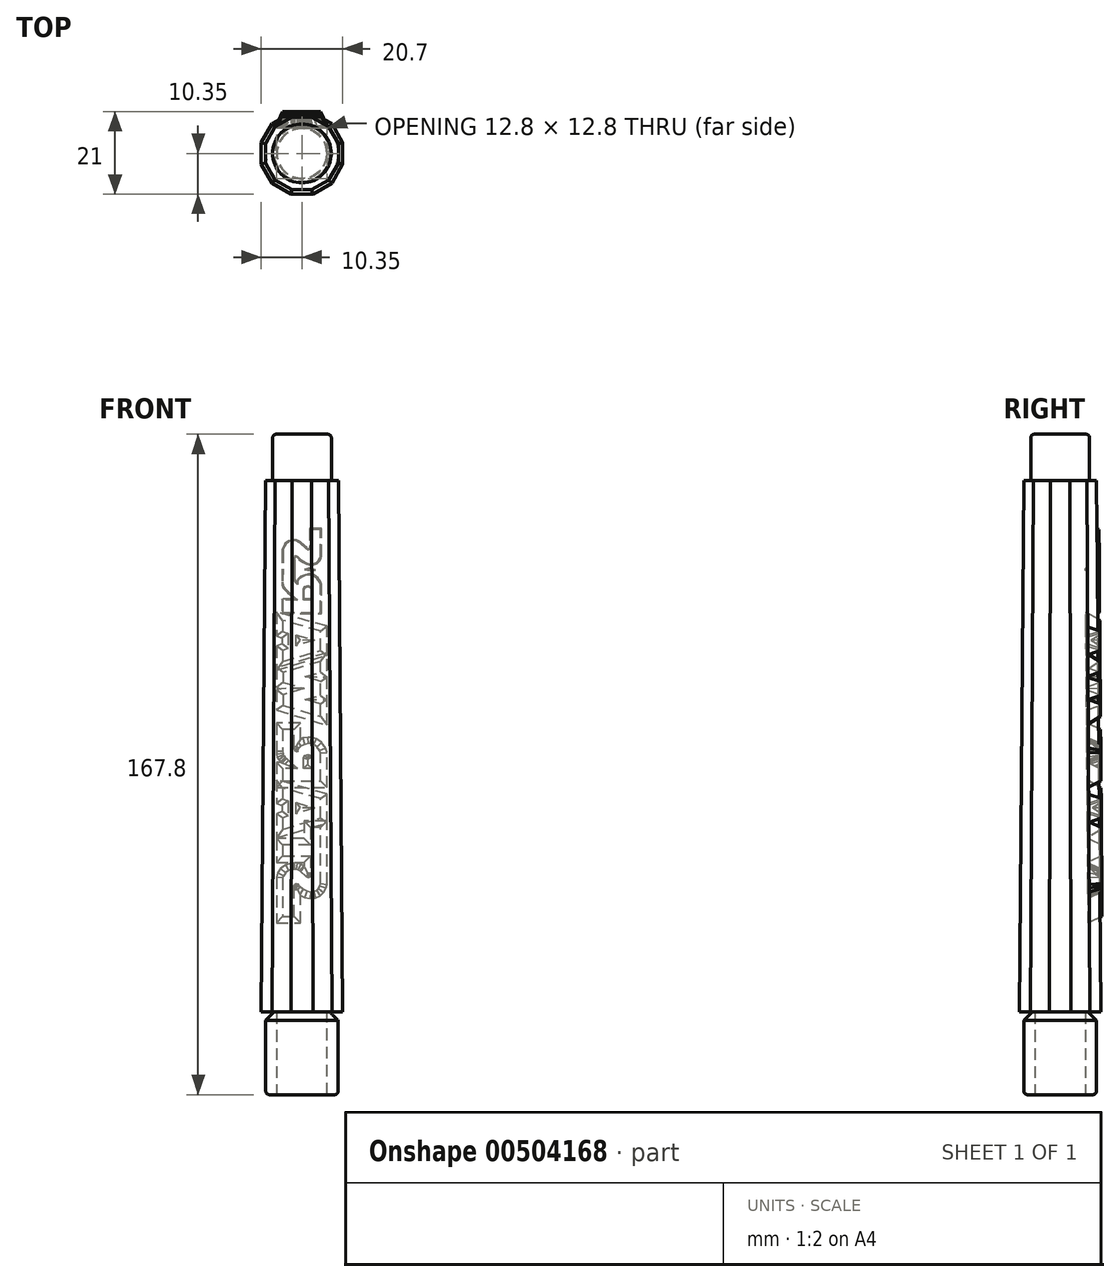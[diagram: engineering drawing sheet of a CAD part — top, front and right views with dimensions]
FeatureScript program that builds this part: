
annotation { "Feature Type Name" : "Feature", "Feature Type Description" : "" }
export const myFeature = defineFeature(function(context is Context, id is Id, definition is map)
    precondition{}
    {
        {
            var Q0;
            Q0=qCreatedBy(makeId("Top.planeOp"),FACE);
            var sketch = newSketch(context, id + "F0", { "sketchPlane" : qUnion([Q0])});
            skCircle(sketch, "E0", {"center": v(0, 0) * mm, "radius": 6.4 * mm});
            skCircle(sketch, "E1", {"center": v(0, 0) * mm, "radius": 9.2 * mm});
            skCircle(sketch, "E2", {"center": v(0, 0) * mm, "radius": 10.35 * mm});
            skSolve(sketch);
        }
        {
            var Q0;
            Q0=qCreatedBy(makeId("Top.planeOp"),FACE);
            cPlane(context, id + "F1", {"entities" : qUnion([Q0]), "cplaneType" : CPlaneType.OFFSET, "offset" : 21 * mm, "width" : 150 * mm, "height" : 150 * mm});
        }
        {
            var Q0;
            Q0=qCreatedBy(id+"F1.planeOp",FACE);
            var sketch = newSketch(context, id + "F2", { "sketchPlane" : qUnion([Q0])});
            skCircle(sketch, "E3", {"center": v(0, 0) * mm, "radius": 6.4 * mm});
            skCircle(sketch, "E4", {"center": v(0, 0) * mm, "radius": 9.2 * mm});
            skCircle(sketch, "E5", {"center": v(0, 0) * mm, "radius": 10.35 * mm});
            skSolve(sketch);
        }
        {
            var Q0;
            Q0=qCreatedBy(id+"F1.planeOp",FACE);
            cPlane(context, id + "F3", {"entities" : qUnion([Q0]), "cplaneType" : CPlaneType.OFFSET, "offset" : 135 * mm, "width" : 150 * mm, "height" : 150 * mm});
        }
        {
            var Q0;
            Q0=qCreatedBy(id+"F3.planeOp",FACE);
            var sketch = newSketch(context, id + "F4", { "sketchPlane" : qUnion([Q0])});
            skPoint(sketch, "E6.0", {"position": v(0, 0) * mm});
            skCircle(sketch, "E7", {"center": v(0, 0) * mm, "radius": 4.9 * mm});
            skCircle(sketch, "E8", {"center": v(0, 0) * mm, "radius": 7.45 * mm});
            skCircle(sketch, "E9", {"center": v(0, 0) * mm, "radius": 9.25 * mm});
            skSolve(sketch);
        }
        {
            var Q0;
            Q0=qCreatedBy(id+"F3.planeOp",FACE);
            cPlane(context, id + "F5", {"entities" : qUnion([Q0]), "cplaneType" : CPlaneType.OFFSET, "offset" : 11.8 * mm, "width" : 150 * mm, "height" : 150 * mm});
        }
        {
            var Q0;
            Q0=qCreatedBy(id+"F5.planeOp",FACE);
            var sketch = newSketch(context, id + "F6", { "sketchPlane" : qUnion([Q0])});
            skPoint(sketch, "E10.0", {"position": v(0, 0) * mm});
            skCircle(sketch, "E11", {"center": v(0, 0) * mm, "radius": 4.9 * mm});
            skCircle(sketch, "E12", {"center": v(0, 0) * mm, "radius": 7.45 * mm});
            skCircle(sketch, "E13", {"center": v(0, 0) * mm, "radius": 9.25 * mm});
            skSolve(sketch);
        }
        {
            var Q0;
            Q0=qCreatedBy(makeId("Front.planeOp"),FACE);
            var sketch = newSketch(context, id + "F7", { "sketchPlane" : qUnion([Q0])});
            skPoint(sketch, "E14.0", {"position": v(0, 167.8) * mm});
            skLineSegment(sketch, "E15", {"start": v(0, 167.8) * mm, "end": v(0, 0) * mm, "construction": true});
            skCircle(sketch, "E16", {"center": v(0, 36.85) * mm, "radius": 2.35 * mm});
            skCircle(sketch, "E17", {"center": v(0, 57.2) * mm, "radius": 2.6 * mm});
            skCircle(sketch, "E18", {"center": v(0, 79.25) * mm, "radius": 2.75 * mm});
            skCircle(sketch, "E19", {"center": v(0, 102.2) * mm, "radius": 2.3 * mm});
            skCircle(sketch, "E20", {"center": v(0, 127.6) * mm, "radius": 3 * mm});
            skCircle(sketch, "E21", {"center": v(2.3, 147.6) * mm, "radius": 2.1 * mm});
            skCircle(sketch, "E22", {"center": v(-3.01, 148.25) * mm, "radius": 1.45 * mm});
            skCircle(sketch, "E23", {"center": v(0, 30.75) * mm, "radius": 2.75 * mm});
            skSolve(sketch);
        }
        {
            var Q0;
            Q0=makeQuery(id+"F0.imprint","IMPRINT",FACE,{"disambiguationData":[TD([[makeQuery(id+"F0.imprint","IMPRINT",EDGE,{"derivedFrom":sQuery(id+"F0.wireOp",EDGE,"E0")}),1.0]])]});
            var Q1;
            Q1=makeQuery(id+"F2.imprint","IMPRINT",FACE,{"disambiguationData":[TD([[makeQuery(id+"F2.imprint","IMPRINT",EDGE,{"derivedFrom":sQuery(id+"F2.wireOp",EDGE,"E3")}),1.0]])]});
            var Q2;
            Q2=makeQuery(id+"F4.imprint","IMPRINT",FACE,{"disambiguationData":[TD([[makeQuery(id+"F4.imprint","IMPRINT",EDGE,{"derivedFrom":sQuery(id+"F4.wireOp",EDGE,"E7")}),1.0]])]});
            var Q3;
            Q3=makeQuery(id+"F6.imprint","IMPRINT",FACE,{"disambiguationData":[TD([[makeQuery(id+"F6.imprint","IMPRINT",EDGE,{"derivedFrom":sQuery(id+"F6.wireOp",EDGE,"E11")}),1.0]])]});
            loft(context, id + "F8", {"sheetProfilesArray" : [{ "sheetProfileEntities" : qUnion([Q0]) }, { "sheetProfileEntities" : qUnion([Q1]) }, { "sheetProfileEntities" : qUnion([Q2]) }, { "sheetProfileEntities" : qUnion([Q3]) }]});
        }
        {
            var Q0;
            Q0=makeQuery(id+"F7.imprint","IMPRINT",FACE,{"disambiguationData":[TD([[makeQuery(id+"F7.imprint","IMPRINT",EDGE,{"derivedFrom":sQuery(id+"F7.wireOp",EDGE,"E23")}),1.0]])]});
            extrude(context, id + "F9", {"entities" : qUnion([Q0]), "operationType" : NewBodyOperationType.ADD, "oppositeDirection" : true, "depth" : 15 * mm});
        }
        {
            var Q0;
            Q0=makeQuery(id+"F7.imprint","IMPRINT",FACE,{"disambiguationData":[TD([[makeQuery(id+"F7.imprint","IMPRINT",EDGE,{"derivedFrom":sQuery(id+"F7.wireOp",EDGE,"E16")}),1.0]])]});
            var Q1;
            Q1=makeQuery(id+"F7.imprint","IMPRINT",FACE,{"disambiguationData":[TD([[makeQuery(id+"F7.imprint","IMPRINT",EDGE,{"derivedFrom":sQuery(id+"F7.wireOp",EDGE,"E17")}),1.0]])]});
            var Q2;
            Q2=makeQuery(id+"F7.imprint","IMPRINT",FACE,{"disambiguationData":[TD([[makeQuery(id+"F7.imprint","IMPRINT",EDGE,{"derivedFrom":sQuery(id+"F7.wireOp",EDGE,"E18")}),1.0]])]});
            var Q3;
            Q3=makeQuery(id+"F7.imprint","IMPRINT",FACE,{"disambiguationData":[TD([[makeQuery(id+"F7.imprint","IMPRINT",EDGE,{"derivedFrom":sQuery(id+"F7.wireOp",EDGE,"E19")}),1.0]])]});
            var Q4;
            Q4=makeQuery(id+"F7.imprint","IMPRINT",FACE,{"disambiguationData":[TD([[makeQuery(id+"F7.imprint","IMPRINT",EDGE,{"derivedFrom":sQuery(id+"F7.wireOp",EDGE,"E20")}),1.0]])]});
            var Q5;
            Q5=makeQuery(id+"F7.imprint","IMPRINT",FACE,{"disambiguationData":[TD([[makeQuery(id+"F7.imprint","IMPRINT",EDGE,{"derivedFrom":sQuery(id+"F7.wireOp",EDGE,"E21")}),1.0]])]});
            var Q6;
            Q6=makeQuery(id+"F7.imprint","IMPRINT",FACE,{"disambiguationData":[TD([[makeQuery(id+"F7.imprint","IMPRINT",EDGE,{"derivedFrom":sQuery(id+"F7.wireOp",EDGE,"E22")}),1.0]])]});
            extrude(context, id + "F10", {"entities" : qUnion([Q0, Q1, Q2, Q3, Q4, Q5, Q6]), "operationType" : NewBodyOperationType.ADD, "depth" : 15 * mm});
        }
        {
            var Q0;
            Q0=makeQuery(id+"F0.imprint","IMPRINT",FACE,{"disambiguationData":[TD([[makeQuery(id+"F0.imprint","IMPRINT",EDGE,{"derivedFrom":sQuery(id+"F0.wireOp",EDGE,"E0")}),-1.0]])]});
            var Q1;
            Q1=makeQuery(id+"F0.imprint","IMPRINT",FACE,{"disambiguationData":[TD([[makeQuery(id+"F0.imprint","IMPRINT",EDGE,{"derivedFrom":sQuery(id+"F0.wireOp",EDGE,"E0")}),1.0]])]});
            extrude(context, id + "F11", {"entities" : qUnion([Q0, Q1]), "depth" : 21 * mm});
        }
        {
            var Q0;
            Q0=makeQuery(id+"F6.imprint","IMPRINT",FACE,{"disambiguationData":[TD([[makeQuery(id+"F6.imprint","IMPRINT",EDGE,{"derivedFrom":sQuery(id+"F6.wireOp",EDGE,"E11")}),-1.0]])]});
            var Q1;
            Q1=makeQuery(id+"F6.imprint","IMPRINT",FACE,{"disambiguationData":[TD([[makeQuery(id+"F6.imprint","IMPRINT",EDGE,{"derivedFrom":sQuery(id+"F6.wireOp",EDGE,"E11")}),1.0]])]});
            extrude(context, id + "F12", {"entities" : qUnion([Q0, Q1]), "oppositeDirection" : true, "depth" : 11.8 * mm});
        }
        {
            var Q0;
            Q0=qCreatedBy(id+"F1.planeOp",FACE);
            var sketch = newSketch(context, id + "F13", { "sketchPlane" : qUnion([Q0])});
            skPoint(sketch, "E24.0", {"position": v(0, 0) * mm});
            skLineSegment(sketch, "E25.0", {"start": v(-2.77, 10.35) * mm, "end": v(2.77, 10.35) * mm});
            skLineSegment(sketch, "E25.1", {"start": v(2.77, 10.35) * mm, "end": v(7.58, 7.58) * mm});
            skLineSegment(sketch, "E25.2", {"start": v(7.58, 7.58) * mm, "end": v(10.35, 2.77) * mm});
            skLineSegment(sketch, "E25.3", {"start": v(10.35, 2.77) * mm, "end": v(10.35, -2.77) * mm});
            skLineSegment(sketch, "E25.4", {"start": v(10.35, -2.77) * mm, "end": v(7.58, -7.58) * mm});
            skLineSegment(sketch, "E25.5", {"start": v(7.58, -7.58) * mm, "end": v(2.77, -10.35) * mm});
            skLineSegment(sketch, "E25.6", {"start": v(2.77, -10.35) * mm, "end": v(-2.77, -10.35) * mm});
            skLineSegment(sketch, "E25.7", {"start": v(-2.77, -10.35) * mm, "end": v(-7.58, -7.58) * mm});
            skLineSegment(sketch, "E25.8", {"start": v(-7.58, -7.58) * mm, "end": v(-10.35, -2.77) * mm});
            skLineSegment(sketch, "E25.9", {"start": v(-10.35, -2.77) * mm, "end": v(-10.35, 2.77) * mm});
            skLineSegment(sketch, "E25.10", {"start": v(-10.35, 2.77) * mm, "end": v(-7.58, 7.58) * mm});
            skLineSegment(sketch, "E25.11", {"start": v(-7.58, 7.58) * mm, "end": v(-2.77, 10.35) * mm});
            skPoint(sketch, "E25.0.midPoint", {"position": v(0, 10.35) * mm});
            skSolve(sketch);
        }
        {
            var Q0;
            Q0=qCreatedBy(id+"F3.planeOp",FACE);
            var sketch = newSketch(context, id + "F14", { "sketchPlane" : qUnion([Q0])});
            skPoint(sketch, "E26.0", {"position": v(0, 0) * mm});
            skLineSegment(sketch, "E27.0", {"start": v(-2.48, 9.25) * mm, "end": v(2.48, 9.25) * mm});
            skLineSegment(sketch, "E27.1", {"start": v(2.48, 9.25) * mm, "end": v(6.77, 6.77) * mm});
            skLineSegment(sketch, "E27.2", {"start": v(6.77, 6.77) * mm, "end": v(9.25, 2.48) * mm});
            skLineSegment(sketch, "E27.3", {"start": v(9.25, 2.48) * mm, "end": v(9.25, -2.48) * mm});
            skLineSegment(sketch, "E27.4", {"start": v(9.25, -2.48) * mm, "end": v(6.77, -6.77) * mm});
            skLineSegment(sketch, "E27.5", {"start": v(6.77, -6.77) * mm, "end": v(2.48, -9.25) * mm});
            skLineSegment(sketch, "E27.6", {"start": v(2.48, -9.25) * mm, "end": v(-2.48, -9.25) * mm});
            skLineSegment(sketch, "E27.7", {"start": v(-2.48, -9.25) * mm, "end": v(-6.77, -6.77) * mm});
            skLineSegment(sketch, "E27.8", {"start": v(-6.77, -6.77) * mm, "end": v(-9.25, -2.48) * mm});
            skLineSegment(sketch, "E27.9", {"start": v(-9.25, -2.48) * mm, "end": v(-9.25, 2.48) * mm});
            skLineSegment(sketch, "E27.10", {"start": v(-9.25, 2.48) * mm, "end": v(-6.77, 6.77) * mm});
            skLineSegment(sketch, "E27.11", {"start": v(-6.77, 6.77) * mm, "end": v(-2.48, 9.25) * mm});
            skPoint(sketch, "E27.0.midPoint", {"position": v(0, 9.25) * mm});
            skSolve(sketch);
        }
        {
            var Q0;
            Q0=makeQuery(id+"F13.imprint","IMPRINT",FACE,{"disambiguationData":[TD([[makeQuery(id+"F13.imprint","IMPRINT",EDGE,{"derivedFrom":sQuery(id+"F13.wireOp",EDGE,"E25.0")}),-1.0]])]});
            var Q1;
            Q1=makeQuery(id+"F14.imprint","IMPRINT",FACE,{"disambiguationData":[TD([[makeQuery(id+"F14.imprint","IMPRINT",EDGE,{"derivedFrom":sQuery(id+"F14.wireOp",EDGE,"E27.0")}),-1.0]])]});
            loft(context, id + "F15", {"sheetProfilesArray" : [{ "sheetProfileEntities" : qUnion([Q0]) }, { "sheetProfileEntities" : qUnion([Q1]) }]});
        }
        {
            var Q0;
            Q0=makeQuery(id+"F8.opLoft","SWEPT_BODY",BODY,{"disambiguationData":[OSD([makeQuery(id+"F0.imprint","IMPRINT",FACE,{"disambiguationData":[TD([[makeQuery(id+"F0.imprint","IMPRINT",EDGE,{"derivedFrom":sQuery(id+"F0.wireOp",EDGE,"E0")}),1.0]])]}),sQuery(id+"F2.wireOp",EDGE,"E3"),sQuery(id+"F4.wireOp",EDGE,"E7"),makeQuery(id+"F6.imprint","IMPRINT",FACE,{"disambiguationData":[TD([[makeQuery(id+"F6.imprint","IMPRINT",EDGE,{"derivedFrom":sQuery(id+"F6.wireOp",EDGE,"E11")}),1.0]])]})])]});
            var Q1;
            Q1=makeQuery(id+"F11.opExtrude","SWEPT_BODY",BODY,{"disambiguationData":[OSD([sQuery(id+"F0.wireOp",EDGE,"E1")])]});
            booleanBodies(context, id + "F16", {"operationType" : BooleanOperationType.SUBTRACTION, "tools" : qUnion([Q0]), "targets" : qUnion([Q1])});
        }
        {
            var Q0;
            Q0=qCreatedBy(makeId("Right.planeOp"),FACE);
            var sketch = newSketch(context, id + "F17", { "sketchPlane" : qUnion([Q0])});
            skPoint(sketch, "E28.0", {"position": v(-8.22, 147.6) * mm});
            skLineSegment(sketch, "E29", {"start": v(-8.22, 147.6) * mm, "end": v(-17.72, 147.6) * mm});
            skCircle(sketch, "E30", {"center": v(-17.72, 147.6) * mm, "radius": 10 * mm});
            skSolve(sketch);
        }
        {
            var Q0;
            Q0=makeQuery(id+"F17.imprint","IMPRINT",FACE,{"disambiguationData":[TD([[makeQuery(id+"F17.imprint","IMPRINT",EDGE,{"derivedFrom":sQuery(id+"F17.wireOp",EDGE,"E30")}),1.0]])]});
            extrude(context, id + "F18", {"entities" : qUnion([Q0]), "endBound" : BoundingType.SYMMETRIC, "oppositeDirection" : true, "depth" : 15 * mm});
        }
        {
            var Q0;
            Q0=makeQuery(id+"F18.opExtrude","SWEPT_BODY",BODY,{"disambiguationData":[OSD([sQuery(id+"F17.wireOp",EDGE,"E30")])]});
            var Q1;
            Q1=makeQuery(id+"F11.opExtrude","SWEPT_BODY",BODY,{"disambiguationData":[OSD([sQuery(id+"F0.wireOp",EDGE,"E1")])]});
            booleanBodies(context, id + "F19", {"operationType" : BooleanOperationType.SUBTRACTION, "tools" : qUnion([Q0]), "targets" : qUnion([Q1])});
        }
        {
            var Q0;
            Q0=makeQuery(id+"F11.opExtrude","CAP_EDGE",EDGE,{"disambiguationData":[OSD([sQuery(id+"F0.wireOp",EDGE,"E1")])],"isStart":false});
            chamfer(context, id + "F20", {"entities" : qUnion([Q0]), "width" : 2.15 * mm, "tangentPropagation" : true});
        }
        {
            var Q0;
            Q0=makeQuery(id+"F12.opExtrude","CAP_EDGE",EDGE,{"disambiguationData":[OSD([sQuery(id+"F6.wireOp",EDGE,"E12")])],"isStart":true});
            var Q1;
            Q1=makeQuery(id+"F11.opExtrude","CAP_EDGE",EDGE,{"disambiguationData":[OSD([sQuery(id+"F0.wireOp",EDGE,"E1")])],"isStart":true});
            fillet(context, id + "F21", {"entities" : qUnion([Q0, Q1]), "radius" : 0.9 * mm, "tangentPropagation" : true, "allowEdgeOverflow" : false});
        }
        {
            var Q0;
            Q0=makeQuery(id+"F15.opLoft","SWEPT_FACE",FACE,{"disambiguationData":[OSD([sQuery(id+"F13.wireOp",EDGE,"E25.0"),sQuery(id+"F13.wireOp",EDGE,"E25.1"),sQuery(id+"F13.wireOp",EDGE,"E25.11"),sQuery(id+"F14.wireOp",EDGE,"E27.0"),sQuery(id+"F14.wireOp",EDGE,"E27.1"),sQuery(id+"F14.wireOp",EDGE,"E27.11")])]});
            var sketch = newSketch(context, id + "F22", { "sketchPlane" : qUnion([Q0])});
            skLineSegment(sketch, "E31", {"start": v(-1.96, 139.37) * mm, "end": v(-1.96, 139.26) * mm});
            skLineSegment(sketch, "E32", {"start": v(-1.96, 139.26) * mm, "end": v(-1.94, 138.93) * mm});
            skLineSegment(sketch, "E33", {"start": v(-1.94, 138.93) * mm, "end": v(-1.84, 138.6) * mm});
            skLineSegment(sketch, "E34", {"start": v(-1.84, 138.6) * mm, "end": v(-1.62, 138.53) * mm});
            skLineSegment(sketch, "E35", {"start": v(-1.62, 138.53) * mm, "end": v(-1.3, 138.74) * mm});
            skLineSegment(sketch, "E36", {"start": v(-1.3, 138.74) * mm, "end": v(-1.22, 138.83) * mm});
            skLineSegment(sketch, "E37", {"start": v(-1.22, 138.83) * mm, "end": v(0.26, 140.08) * mm});
            skLineSegment(sketch, "E38", {"start": v(0.26, 140.08) * mm, "end": v(0.4, 140.21) * mm});
            skLineSegment(sketch, "E39", {"start": v(0.4, 140.21) * mm, "end": v(0.87, 140.56) * mm});
            skLineSegment(sketch, "E40", {"start": v(0.87, 140.56) * mm, "end": v(1.35, 140.8) * mm});
            skLineSegment(sketch, "E41", {"start": v(1.35, 140.8) * mm, "end": v(1.8, 140.88) * mm});
            skLineSegment(sketch, "E42", {"start": v(1.8, 140.88) * mm, "end": v(2.15, 140.9) * mm});
            skLineSegment(sketch, "E43", {"start": v(2.15, 140.9) * mm, "end": v(2.27, 140.9) * mm});
            skLineSegment(sketch, "E44", {"start": v(2.27, 140.9) * mm, "end": v(2.57, 140.9) * mm});
            skLineSegment(sketch, "E45", {"start": v(2.57, 140.9) * mm, "end": v(3.44, 140.6) * mm});
            skLineSegment(sketch, "E46", {"start": v(3.44, 140.6) * mm, "end": v(4.32, 139.89) * mm});
            skLineSegment(sketch, "E47", {"start": v(4.32, 139.89) * mm, "end": v(4.87, 138.96) * mm});
            skLineSegment(sketch, "E48", {"start": v(4.87, 138.96) * mm, "end": v(5.07, 138.27) * mm});
            skLineSegment(sketch, "E49", {"start": v(5.07, 138.27) * mm, "end": v(5.07, 138.03) * mm});
            skLineSegment(sketch, "E50", {"start": v(5.07, 138.03) * mm, "end": v(5.12, 130.13) * mm});
            skLineSegment(sketch, "E51", {"start": v(5.12, 130.13) * mm, "end": v(5.12, 129.96) * mm});
            skLineSegment(sketch, "E52", {"start": v(5.12, 129.96) * mm, "end": v(5.1, 129.47) * mm});
            skLineSegment(sketch, "E53", {"start": v(5.1, 129.47) * mm, "end": v(5, 129.04) * mm});
            skLineSegment(sketch, "E54", {"start": v(5, 129.04) * mm, "end": v(4.75, 128.66) * mm});
            skLineSegment(sketch, "E55", {"start": v(4.75, 128.66) * mm, "end": v(4.43, 128.28) * mm});
            skLineSegment(sketch, "E56", {"start": v(4.43, 128.28) * mm, "end": v(4.32, 128.16) * mm});
            skLineSegment(sketch, "E57", {"start": v(4.32, 128.16) * mm, "end": v(4.15, 127.98) * mm});
            skLineSegment(sketch, "E58", {"start": v(4.15, 127.98) * mm, "end": v(3.6, 127.46) * mm});
            skLineSegment(sketch, "E59", {"start": v(3.6, 127.46) * mm, "end": v(2.77, 126.69) * mm});
            skLineSegment(sketch, "E60", {"start": v(2.77, 126.69) * mm, "end": v(2.07, 126.07) * mm});
            skLineSegment(sketch, "E61", {"start": v(2.07, 126.07) * mm, "end": v(1.77, 125.82) * mm});
            skLineSegment(sketch, "E62", {"start": v(1.77, 125.82) * mm, "end": v(5.12, 125.82) * mm});
            skLineSegment(sketch, "E63", {"start": v(5.12, 125.82) * mm, "end": v(5.12, 122.2) * mm});
            skLineSegment(sketch, "E64", {"start": v(5.12, 122.2) * mm, "end": v(-4.92, 122.2) * mm});
            skLineSegment(sketch, "E65", {"start": v(-4.92, 122.2) * mm, "end": v(-4.92, 123.14) * mm});
            skLineSegment(sketch, "E66", {"start": v(-4.92, 123.14) * mm, "end": v(-4.92, 125.29) * mm});
            skLineSegment(sketch, "E67", {"start": v(-4.92, 125.29) * mm, "end": v(-4.92, 127.67) * mm});
            skLineSegment(sketch, "E68", {"start": v(-4.92, 127.67) * mm, "end": v(-4.92, 128.9) * mm});
            skLineSegment(sketch, "E69", {"start": v(-4.92, 128.9) * mm, "end": v(-4.92, 129.32) * mm});
            skLineSegment(sketch, "E70", {"start": v(-4.92, 129.32) * mm, "end": v(-4.92, 129.57) * mm});
            skLineSegment(sketch, "E71", {"start": v(-4.92, 129.57) * mm, "end": v(-4.68, 130.3) * mm});
            skLineSegment(sketch, "E72", {"start": v(-4.68, 130.3) * mm, "end": v(-4.02, 131.23) * mm});
            skLineSegment(sketch, "E73", {"start": v(-4.02, 131.23) * mm, "end": v(-3.07, 131.91) * mm});
            skLineSegment(sketch, "E74", {"start": v(-3.07, 131.91) * mm, "end": v(-2.2, 132.18) * mm});
            skLineSegment(sketch, "E75", {"start": v(-2.2, 132.18) * mm, "end": v(-1.9, 132.18) * mm});
            skLineSegment(sketch, "E76", {"start": v(-1.9, 132.18) * mm, "end": v(-1.61, 132.18) * mm});
            skLineSegment(sketch, "E77", {"start": v(-1.61, 132.18) * mm, "end": v(-0.72, 132.01) * mm});
            skLineSegment(sketch, "E78", {"start": v(-0.72, 132.01) * mm, "end": v(0.3, 131.56) * mm});
            skLineSegment(sketch, "E79", {"start": v(0.3, 131.56) * mm, "end": v(1.03, 130.9) * mm});
            skLineSegment(sketch, "E80", {"start": v(1.03, 130.9) * mm, "end": v(1.3, 130.32) * mm});
            skLineSegment(sketch, "E81", {"start": v(1.3, 130.32) * mm, "end": v(1.3, 130.13) * mm});
            skLineSegment(sketch, "E82", {"start": v(1.3, 130.13) * mm, "end": v(1.38, 130.21) * mm});
            skLineSegment(sketch, "E83", {"start": v(1.38, 130.21) * mm, "end": v(1.55, 130.46) * mm});
            skLineSegment(sketch, "E84", {"start": v(1.55, 130.46) * mm, "end": v(1.71, 130.87) * mm});
            skLineSegment(sketch, "E85", {"start": v(1.71, 130.87) * mm, "end": v(1.79, 131.27) * mm});
            skLineSegment(sketch, "E86", {"start": v(1.79, 131.27) * mm, "end": v(1.79, 131.4) * mm});
            skLineSegment(sketch, "E87", {"start": v(1.79, 131.4) * mm, "end": v(1.79, 131.64) * mm});
            skLineSegment(sketch, "E88", {"start": v(1.79, 131.64) * mm, "end": v(1.79, 132.35) * mm});
            skLineSegment(sketch, "E89", {"start": v(1.79, 132.35) * mm, "end": v(1.79, 133.65) * mm});
            skLineSegment(sketch, "E90", {"start": v(1.79, 133.65) * mm, "end": v(1.79, 134.8) * mm});
            skLineSegment(sketch, "E91", {"start": v(1.79, 134.8) * mm, "end": v(1.79, 135.3) * mm});
            skLineSegment(sketch, "E92", {"start": v(1.79, 135.3) * mm, "end": v(1.79, 135.34) * mm});
            skLineSegment(sketch, "E93", {"start": v(1.79, 135.34) * mm, "end": v(1.8, 135.45) * mm});
            skLineSegment(sketch, "E94", {"start": v(1.8, 135.45) * mm, "end": v(1.82, 135.7) * mm});
            skLineSegment(sketch, "E95", {"start": v(1.82, 135.7) * mm, "end": v(1.83, 136) * mm});
            skLineSegment(sketch, "E96", {"start": v(1.83, 136) * mm, "end": v(1.8, 136.3) * mm});
            skLineSegment(sketch, "E97", {"start": v(1.8, 136.3) * mm, "end": v(1.72, 136.52) * mm});
            skLineSegment(sketch, "E98", {"start": v(1.72, 136.52) * mm, "end": v(1.56, 136.6) * mm});
            skLineSegment(sketch, "E99", {"start": v(1.56, 136.6) * mm, "end": v(1.3, 136.5) * mm});
            skLineSegment(sketch, "E100", {"start": v(1.3, 136.5) * mm, "end": v(1, 136.25) * mm});
            skLineSegment(sketch, "E101", {"start": v(1, 136.25) * mm, "end": v(0.92, 136.15) * mm});
            skLineSegment(sketch, "E102", {"start": v(0.92, 136.15) * mm, "end": v(0.69, 135.9) * mm});
            skLineSegment(sketch, "E103", {"start": v(0.69, 135.9) * mm, "end": v(-0.1, 135.24) * mm});
            skLineSegment(sketch, "E104", {"start": v(-0.1, 135.24) * mm, "end": v(-1.14, 134.7) * mm});
            skLineSegment(sketch, "E105", {"start": v(-1.14, 134.7) * mm, "end": v(-2.13, 134.5) * mm});
            skLineSegment(sketch, "E106", {"start": v(-2.13, 134.5) * mm, "end": v(-3.04, 134.6) * mm});
            skLineSegment(sketch, "E107", {"start": v(-3.04, 134.6) * mm, "end": v(-3.82, 134.92) * mm});
            skLineSegment(sketch, "E108", {"start": v(-3.82, 134.92) * mm, "end": v(-4.44, 135.45) * mm});
            skLineSegment(sketch, "E109", {"start": v(-4.44, 135.45) * mm, "end": v(-4.83, 136.14) * mm});
            skLineSegment(sketch, "E110", {"start": v(-4.83, 136.14) * mm, "end": v(-4.98, 136.74) * mm});
            skLineSegment(sketch, "E111", {"start": v(-4.98, 136.74) * mm, "end": v(-4.98, 136.94) * mm});
            skLineSegment(sketch, "E112", {"start": v(-4.98, 136.94) * mm, "end": v(-4.98, 143.7) * mm});
            skLineSegment(sketch, "E113", {"start": v(-4.98, 143.7) * mm, "end": v(-1.96, 143.7) * mm});
            skLineSegment(sketch, "E114", {"start": v(-1.96, 143.7) * mm, "end": v(-1.96, 139.37) * mm});
            skLineSegment(sketch, "E115", {"start": v(-4.92, 117.9) * mm, "end": v(-4.92, 112.62) * mm});
            skLineSegment(sketch, "E116", {"start": v(-4.92, 112.62) * mm, "end": v(5.12, 109.66) * mm});
            skLineSegment(sketch, "E117", {"start": v(5.12, 109.66) * mm, "end": v(5.12, 112.96) * mm});
            skLineSegment(sketch, "E118", {"start": v(5.12, 112.96) * mm, "end": v(3.72, 113.5) * mm});
            skLineSegment(sketch, "E119", {"start": v(3.72, 113.5) * mm, "end": v(3.72, 116.97) * mm});
            skLineSegment(sketch, "E120", {"start": v(3.72, 116.97) * mm, "end": v(5.12, 117.49) * mm});
            skLineSegment(sketch, "E121", {"start": v(5.12, 117.49) * mm, "end": v(5.12, 120.72) * mm});
            skLineSegment(sketch, "E122", {"start": v(5.12, 120.72) * mm, "end": v(-4.92, 117.9) * mm});
            skLineSegment(sketch, "E123", {"start": v(1.3, 114.23) * mm, "end": v(-2.38, 115.37) * mm});
            skLineSegment(sketch, "E124", {"start": v(-2.38, 115.37) * mm, "end": v(1.3, 116.44) * mm});
            skLineSegment(sketch, "E125", {"start": v(1.3, 116.44) * mm, "end": v(1.3, 114.23) * mm});
            skLineSegment(sketch, "E126", {"start": v(-4.98, 95.7) * mm, "end": v(-4.98, 99.4) * mm});
            skLineSegment(sketch, "E127", {"start": v(-4.98, 99.4) * mm, "end": v(-1.63, 100.35) * mm});
            skLineSegment(sketch, "E128", {"start": v(-1.63, 100.35) * mm, "end": v(-4.98, 101.22) * mm});
            skLineSegment(sketch, "E129", {"start": v(-4.98, 101.22) * mm, "end": v(-4.98, 105.1) * mm});
            skLineSegment(sketch, "E130", {"start": v(-4.98, 105.1) * mm, "end": v(-1.63, 106.1) * mm});
            skLineSegment(sketch, "E131", {"start": v(-1.63, 106.1) * mm, "end": v(-4.98, 107.1) * mm});
            skLineSegment(sketch, "E132", {"start": v(-4.98, 107.1) * mm, "end": v(-4.98, 110.32) * mm});
            skLineSegment(sketch, "E133", {"start": v(-4.98, 110.32) * mm, "end": v(5.07, 107.37) * mm});
            skLineSegment(sketch, "E134", {"start": v(5.07, 107.37) * mm, "end": v(5.07, 104.43) * mm});
            skLineSegment(sketch, "E135", {"start": v(5.07, 104.43) * mm, "end": v(0.31, 103.14) * mm});
            skLineSegment(sketch, "E136", {"start": v(0.31, 103.14) * mm, "end": v(5.07, 101.68) * mm});
            skLineSegment(sketch, "E137", {"start": v(5.07, 101.68) * mm, "end": v(5.07, 98.67) * mm});
            skLineSegment(sketch, "E138", {"start": v(5.07, 98.67) * mm, "end": v(-4.98, 95.7) * mm});
            skLineSegment(sketch, "E139", {"start": v(1.78, 88.55) * mm, "end": v(1.78, 88.36) * mm});
            skLineSegment(sketch, "E140", {"start": v(1.78, 88.36) * mm, "end": v(1.7, 87.81) * mm});
            skLineSegment(sketch, "E141", {"start": v(1.7, 87.81) * mm, "end": v(1.54, 87.44) * mm});
            skLineSegment(sketch, "E142", {"start": v(1.54, 87.44) * mm, "end": v(1.38, 87.3) * mm});
            skLineSegment(sketch, "E143", {"start": v(1.38, 87.3) * mm, "end": v(1.3, 87.28) * mm});
            skLineSegment(sketch, "E144", {"start": v(1.3, 87.28) * mm, "end": v(1.3, 87.47) * mm});
            skLineSegment(sketch, "E145", {"start": v(1.3, 87.47) * mm, "end": v(1.03, 88.06) * mm});
            skLineSegment(sketch, "E146", {"start": v(1.03, 88.06) * mm, "end": v(0.3, 88.71) * mm});
            skLineSegment(sketch, "E147", {"start": v(0.3, 88.71) * mm, "end": v(-0.72, 89.16) * mm});
            skLineSegment(sketch, "E148", {"start": v(-0.72, 89.16) * mm, "end": v(-1.61, 89.33) * mm});
            skLineSegment(sketch, "E149", {"start": v(-1.61, 89.33) * mm, "end": v(-1.9, 89.33) * mm});
            skLineSegment(sketch, "E150", {"start": v(-1.9, 89.33) * mm, "end": v(-2.2, 89.33) * mm});
            skLineSegment(sketch, "E151", {"start": v(-2.2, 89.33) * mm, "end": v(-3.06, 89.06) * mm});
            skLineSegment(sketch, "E152", {"start": v(-3.06, 89.06) * mm, "end": v(-4.02, 88.38) * mm});
            skLineSegment(sketch, "E153", {"start": v(-4.02, 88.38) * mm, "end": v(-4.68, 87.46) * mm});
            skLineSegment(sketch, "E154", {"start": v(-4.68, 87.46) * mm, "end": v(-4.92, 86.72) * mm});
            skLineSegment(sketch, "E155", {"start": v(-4.92, 86.72) * mm, "end": v(-4.92, 86.47) * mm});
            skLineSegment(sketch, "E156", {"start": v(-4.92, 86.47) * mm, "end": v(-4.92, 86.06) * mm});
            skLineSegment(sketch, "E157", {"start": v(-4.92, 86.06) * mm, "end": v(-4.92, 84.82) * mm});
            skLineSegment(sketch, "E158", {"start": v(-4.92, 84.82) * mm, "end": v(-4.92, 82.44) * mm});
            skLineSegment(sketch, "E159", {"start": v(-4.92, 82.44) * mm, "end": v(-4.92, 80.3) * mm});
            skLineSegment(sketch, "E160", {"start": v(-4.92, 80.3) * mm, "end": v(-4.92, 79.36) * mm});
            skLineSegment(sketch, "E161", {"start": v(-4.92, 79.36) * mm, "end": v(5.12, 79.36) * mm});
            skLineSegment(sketch, "E162", {"start": v(5.12, 79.36) * mm, "end": v(5.12, 82.97) * mm});
            skLineSegment(sketch, "E163", {"start": v(5.12, 82.97) * mm, "end": v(1.78, 82.97) * mm});
            skLineSegment(sketch, "E164", {"start": v(1.78, 82.97) * mm, "end": v(2.07, 83.22) * mm});
            skLineSegment(sketch, "E165", {"start": v(2.07, 83.22) * mm, "end": v(2.77, 83.84) * mm});
            skLineSegment(sketch, "E166", {"start": v(2.77, 83.84) * mm, "end": v(3.6, 84.61) * mm});
            skLineSegment(sketch, "E167", {"start": v(3.6, 84.61) * mm, "end": v(4.15, 85.13) * mm});
            skLineSegment(sketch, "E168", {"start": v(4.15, 85.13) * mm, "end": v(4.32, 85.32) * mm});
            skLineSegment(sketch, "E169", {"start": v(4.32, 85.32) * mm, "end": v(4.43, 85.44) * mm});
            skLineSegment(sketch, "E170", {"start": v(4.43, 85.44) * mm, "end": v(4.75, 85.8) * mm});
            skLineSegment(sketch, "E171", {"start": v(4.75, 85.8) * mm, "end": v(5, 86.19) * mm});
            skLineSegment(sketch, "E172", {"start": v(5, 86.19) * mm, "end": v(5.1, 86.62) * mm});
            skLineSegment(sketch, "E173", {"start": v(5.1, 86.62) * mm, "end": v(5.12, 87.11) * mm});
            skLineSegment(sketch, "E174", {"start": v(5.12, 87.11) * mm, "end": v(5.12, 87.28) * mm});
            skLineSegment(sketch, "E175", {"start": v(5.12, 87.28) * mm, "end": v(5.12, 87.61) * mm});
            skLineSegment(sketch, "E176", {"start": v(5.12, 87.61) * mm, "end": v(5.12, 88.62) * mm});
            skLineSegment(sketch, "E177", {"start": v(5.12, 88.62) * mm, "end": v(5.12, 90.52) * mm});
            skLineSegment(sketch, "E178", {"start": v(5.12, 90.52) * mm, "end": v(5.12, 92.22) * mm});
            skLineSegment(sketch, "E179", {"start": v(5.12, 92.22) * mm, "end": v(5.12, 92.95) * mm});
            skLineSegment(sketch, "E180", {"start": v(5.12, 92.95) * mm, "end": v(1.78, 92.95) * mm});
            skLineSegment(sketch, "E181", {"start": v(1.78, 92.95) * mm, "end": v(1.78, 92.44) * mm});
            skLineSegment(sketch, "E182", {"start": v(1.78, 92.44) * mm, "end": v(1.78, 91.23) * mm});
            skLineSegment(sketch, "E183", {"start": v(1.78, 91.23) * mm, "end": v(1.78, 89.77) * mm});
            skLineSegment(sketch, "E184", {"start": v(1.78, 89.77) * mm, "end": v(1.78, 88.85) * mm});
            skLineSegment(sketch, "E185", {"start": v(1.78, 88.85) * mm, "end": v(1.78, 88.55) * mm});
            skLineSegment(sketch, "E186", {"start": v(-0.57, 85.27) * mm, "end": v(-0.57, 85.08) * mm});
            skLineSegment(sketch, "E187", {"start": v(-0.57, 85.08) * mm, "end": v(-0.57, 84.52) * mm});
            skLineSegment(sketch, "E188", {"start": v(-0.57, 84.52) * mm, "end": v(-0.57, 83.78) * mm});
            skLineSegment(sketch, "E189", {"start": v(-0.57, 83.78) * mm, "end": v(-0.57, 83.2) * mm});
            skLineSegment(sketch, "E190", {"start": v(-0.57, 83.2) * mm, "end": v(-0.57, 82.97) * mm});
            skLineSegment(sketch, "E191", {"start": v(-0.57, 82.97) * mm, "end": v(-2.38, 82.97) * mm});
            skLineSegment(sketch, "E192", {"start": v(-2.38, 82.97) * mm, "end": v(-2.38, 83.23) * mm});
            skLineSegment(sketch, "E193", {"start": v(-2.38, 83.23) * mm, "end": v(-2.38, 83.85) * mm});
            skLineSegment(sketch, "E194", {"start": v(-2.38, 83.85) * mm, "end": v(-2.38, 84.6) * mm});
            skLineSegment(sketch, "E195", {"start": v(-2.38, 84.6) * mm, "end": v(-2.38, 85.1) * mm});
            skLineSegment(sketch, "E196", {"start": v(-2.38, 85.1) * mm, "end": v(-2.38, 85.27) * mm});
            skLineSegment(sketch, "E197", {"start": v(-2.38, 85.27) * mm, "end": v(-2.38, 85.42) * mm});
            skLineSegment(sketch, "E198", {"start": v(-2.38, 85.42) * mm, "end": v(-2.1, 85.88) * mm});
            skLineSegment(sketch, "E199", {"start": v(-2.1, 85.88) * mm, "end": v(-1.47, 86.12) * mm});
            skLineSegment(sketch, "E200", {"start": v(-1.47, 86.12) * mm, "end": v(-0.85, 85.94) * mm});
            skLineSegment(sketch, "E201", {"start": v(-0.85, 85.94) * mm, "end": v(-0.57, 85.43) * mm});
            skLineSegment(sketch, "E202", {"start": v(-0.57, 85.43) * mm, "end": v(-0.57, 85.27) * mm});
            skLineSegment(sketch, "E203", {"start": v(-4.92, 75.3) * mm, "end": v(-4.92, 70) * mm});
            skLineSegment(sketch, "E204", {"start": v(-4.92, 70) * mm, "end": v(5.12, 67.04) * mm});
            skLineSegment(sketch, "E205", {"start": v(5.12, 67.04) * mm, "end": v(5.12, 70.34) * mm});
            skLineSegment(sketch, "E206", {"start": v(5.12, 70.34) * mm, "end": v(3.72, 70.87) * mm});
            skLineSegment(sketch, "E207", {"start": v(3.72, 70.87) * mm, "end": v(3.72, 74.36) * mm});
            skLineSegment(sketch, "E208", {"start": v(3.72, 74.36) * mm, "end": v(5.12, 74.87) * mm});
            skLineSegment(sketch, "E209", {"start": v(5.12, 74.87) * mm, "end": v(5.12, 78.1) * mm});
            skLineSegment(sketch, "E210", {"start": v(5.12, 78.1) * mm, "end": v(-4.92, 75.3) * mm});
            skLineSegment(sketch, "E211", {"start": v(1.3, 71.61) * mm, "end": v(-2.38, 72.75) * mm});
            skLineSegment(sketch, "E212", {"start": v(-2.38, 72.75) * mm, "end": v(1.3, 73.82) * mm});
            skLineSegment(sketch, "E213", {"start": v(1.3, 73.82) * mm, "end": v(1.3, 71.61) * mm});
            skLineSegment(sketch, "E214", {"start": v(1.78, 44.95) * mm, "end": v(5.12, 44.95) * mm});
            skLineSegment(sketch, "E215", {"start": v(5.12, 44.95) * mm, "end": v(5.12, 45.33) * mm});
            skLineSegment(sketch, "E216", {"start": v(5.12, 45.33) * mm, "end": v(5.12, 46.32) * mm});
            skLineSegment(sketch, "E217", {"start": v(5.12, 46.32) * mm, "end": v(5.12, 47.75) * mm});
            skLineSegment(sketch, "E218", {"start": v(5.12, 47.75) * mm, "end": v(5.12, 49.42) * mm});
            skLineSegment(sketch, "E219", {"start": v(5.12, 49.42) * mm, "end": v(5.12, 51.14) * mm});
            skLineSegment(sketch, "E220", {"start": v(5.12, 51.14) * mm, "end": v(5.12, 52.73) * mm});
            skLineSegment(sketch, "E221", {"start": v(5.12, 52.73) * mm, "end": v(5.12, 54) * mm});
            skLineSegment(sketch, "E222", {"start": v(5.12, 54) * mm, "end": v(5.12, 54.56) * mm});
            skLineSegment(sketch, "E223", {"start": v(5.12, 54.56) * mm, "end": v(5.12, 54.74) * mm});
            skLineSegment(sketch, "E224", {"start": v(5.12, 54.74) * mm, "end": v(5.12, 54.96) * mm});
            skLineSegment(sketch, "E225", {"start": v(5.12, 54.96) * mm, "end": v(4.93, 55.63) * mm});
            skLineSegment(sketch, "E226", {"start": v(4.93, 55.63) * mm, "end": v(4.38, 56.47) * mm});
            skLineSegment(sketch, "E227", {"start": v(4.38, 56.47) * mm, "end": v(3.5, 57.09) * mm});
            skLineSegment(sketch, "E228", {"start": v(3.5, 57.09) * mm, "end": v(2.62, 57.33) * mm});
            skLineSegment(sketch, "E229", {"start": v(2.62, 57.33) * mm, "end": v(2.33, 57.33) * mm});
            skLineSegment(sketch, "E230", {"start": v(2.33, 57.33) * mm, "end": v(2.2, 57.33) * mm});
            skLineSegment(sketch, "E231", {"start": v(2.2, 57.33) * mm, "end": v(1.84, 57.36) * mm});
            skLineSegment(sketch, "E232", {"start": v(1.84, 57.36) * mm, "end": v(1.37, 57.36) * mm});
            skLineSegment(sketch, "E233", {"start": v(1.37, 57.36) * mm, "end": v(0.86, 57.21) * mm});
            skLineSegment(sketch, "E234", {"start": v(0.86, 57.21) * mm, "end": v(0.39, 56.9) * mm});
            skLineSegment(sketch, "E235", {"start": v(0.39, 56.9) * mm, "end": v(0.25, 56.78) * mm});
            skLineSegment(sketch, "E236", {"start": v(0.25, 56.78) * mm, "end": v(-1.24, 55.53) * mm});
            skLineSegment(sketch, "E237", {"start": v(-1.24, 55.53) * mm, "end": v(-1.32, 55.44) * mm});
            skLineSegment(sketch, "E238", {"start": v(-1.32, 55.44) * mm, "end": v(-1.63, 55.25) * mm});
            skLineSegment(sketch, "E239", {"start": v(-1.63, 55.25) * mm, "end": v(-1.83, 55.38) * mm});
            skLineSegment(sketch, "E240", {"start": v(-1.83, 55.38) * mm, "end": v(-1.9, 55.75) * mm});
            skLineSegment(sketch, "E241", {"start": v(-1.9, 55.75) * mm, "end": v(-1.9, 56.1) * mm});
            skLineSegment(sketch, "E242", {"start": v(-1.9, 56.1) * mm, "end": v(-1.9, 56.21) * mm});
            skLineSegment(sketch, "E243", {"start": v(-1.9, 56.21) * mm, "end": v(-1.9, 56.28) * mm});
            skLineSegment(sketch, "E244", {"start": v(-1.9, 56.28) * mm, "end": v(-1.9, 56.49) * mm});
            skLineSegment(sketch, "E245", {"start": v(-1.9, 56.49) * mm, "end": v(-1.9, 57) * mm});
            skLineSegment(sketch, "E246", {"start": v(-1.9, 57) * mm, "end": v(-1.9, 57.67) * mm});
            skLineSegment(sketch, "E247", {"start": v(-1.9, 57.67) * mm, "end": v(-1.9, 58.4) * mm});
            skLineSegment(sketch, "E248", {"start": v(-1.9, 58.4) * mm, "end": v(-1.9, 59.13) * mm});
            skLineSegment(sketch, "E249", {"start": v(-1.9, 59.13) * mm, "end": v(-1.9, 59.75) * mm});
            skLineSegment(sketch, "E250", {"start": v(-1.9, 59.75) * mm, "end": v(-1.9, 60.18) * mm});
            skLineSegment(sketch, "E251", {"start": v(-1.9, 60.18) * mm, "end": v(-1.9, 60.35) * mm});
            skLineSegment(sketch, "E252", {"start": v(-1.9, 60.35) * mm, "end": v(5.12, 60.35) * mm});
            skLineSegment(sketch, "E253", {"start": v(5.12, 60.35) * mm, "end": v(5.12, 63.63) * mm});
            skLineSegment(sketch, "E254", {"start": v(5.12, 63.63) * mm, "end": v(-1.9, 63.63) * mm});
            skLineSegment(sketch, "E255", {"start": v(-1.9, 63.63) * mm, "end": v(-1.9, 68.05) * mm});
            skLineSegment(sketch, "E256", {"start": v(-1.9, 68.05) * mm, "end": v(-4.92, 68.05) * mm});
            skLineSegment(sketch, "E257", {"start": v(-4.92, 68.05) * mm, "end": v(-4.92, 53.74) * mm});
            skLineSegment(sketch, "E258", {"start": v(-4.92, 53.74) * mm, "end": v(-4.92, 53.53) * mm});
            skLineSegment(sketch, "E259", {"start": v(-4.92, 53.53) * mm, "end": v(-4.78, 52.92) * mm});
            skLineSegment(sketch, "E260", {"start": v(-4.78, 52.92) * mm, "end": v(-4.4, 52.2) * mm});
            skLineSegment(sketch, "E261", {"start": v(-4.4, 52.2) * mm, "end": v(-3.8, 51.65) * mm});
            skLineSegment(sketch, "E262", {"start": v(-3.8, 51.65) * mm, "end": v(-3.03, 51.3) * mm});
            skLineSegment(sketch, "E263", {"start": v(-3.03, 51.3) * mm, "end": v(-2.14, 51.2) * mm});
            skLineSegment(sketch, "E264", {"start": v(-2.14, 51.2) * mm, "end": v(-1.16, 51.4) * mm});
            skLineSegment(sketch, "E265", {"start": v(-1.16, 51.4) * mm, "end": v(-0.13, 51.93) * mm});
            skLineSegment(sketch, "E266", {"start": v(-0.13, 51.93) * mm, "end": v(0.67, 52.6) * mm});
            skLineSegment(sketch, "E267", {"start": v(0.67, 52.6) * mm, "end": v(0.9, 52.85) * mm});
            skLineSegment(sketch, "E268", {"start": v(0.9, 52.85) * mm, "end": v(0.99, 52.94) * mm});
            skLineSegment(sketch, "E269", {"start": v(0.99, 52.94) * mm, "end": v(1.29, 53.2) * mm});
            skLineSegment(sketch, "E270", {"start": v(1.29, 53.2) * mm, "end": v(1.55, 53.3) * mm});
            skLineSegment(sketch, "E271", {"start": v(1.55, 53.3) * mm, "end": v(1.7, 53.21) * mm});
            skLineSegment(sketch, "E272", {"start": v(1.7, 53.21) * mm, "end": v(1.79, 53) * mm});
            skLineSegment(sketch, "E273", {"start": v(1.79, 53) * mm, "end": v(1.82, 52.7) * mm});
            skLineSegment(sketch, "E274", {"start": v(1.82, 52.7) * mm, "end": v(1.8, 52.4) * mm});
            skLineSegment(sketch, "E275", {"start": v(1.8, 52.4) * mm, "end": v(1.79, 52.14) * mm});
            skLineSegment(sketch, "E276", {"start": v(1.79, 52.14) * mm, "end": v(1.78, 52.03) * mm});
            skLineSegment(sketch, "E277", {"start": v(1.78, 52.03) * mm, "end": v(1.78, 52) * mm});
            skLineSegment(sketch, "E278", {"start": v(1.78, 52) * mm, "end": v(1.78, 51.61) * mm});
            skLineSegment(sketch, "E279", {"start": v(1.78, 51.61) * mm, "end": v(1.78, 50.47) * mm});
            skLineSegment(sketch, "E280", {"start": v(1.78, 50.47) * mm, "end": v(1.78, 48.1) * mm});
            skLineSegment(sketch, "E281", {"start": v(1.78, 48.1) * mm, "end": v(1.78, 45.91) * mm});
            skLineSegment(sketch, "E282", {"start": v(1.78, 45.91) * mm, "end": v(1.78, 44.95) * mm});
            skLineSegment(sketch, "E283", {"start": v(-0.57, 128.12) * mm, "end": v(-0.57, 127.93) * mm});
            skLineSegment(sketch, "E284", {"start": v(-0.57, 127.93) * mm, "end": v(-0.57, 127.37) * mm});
            skLineSegment(sketch, "E285", {"start": v(-0.57, 127.37) * mm, "end": v(-0.57, 126.62) * mm});
            skLineSegment(sketch, "E286", {"start": v(-0.57, 126.62) * mm, "end": v(-0.57, 126.05) * mm});
            skLineSegment(sketch, "E287", {"start": v(-0.57, 126.05) * mm, "end": v(-0.57, 125.82) * mm});
            skLineSegment(sketch, "E288", {"start": v(-0.57, 125.82) * mm, "end": v(-2.38, 125.82) * mm});
            skLineSegment(sketch, "E289", {"start": v(-2.38, 125.82) * mm, "end": v(-2.38, 126.08) * mm});
            skLineSegment(sketch, "E290", {"start": v(-2.38, 126.08) * mm, "end": v(-2.38, 126.7) * mm});
            skLineSegment(sketch, "E291", {"start": v(-2.38, 126.7) * mm, "end": v(-2.38, 127.45) * mm});
            skLineSegment(sketch, "E292", {"start": v(-2.38, 127.45) * mm, "end": v(-2.38, 127.95) * mm});
            skLineSegment(sketch, "E293", {"start": v(-2.38, 127.95) * mm, "end": v(-2.38, 128.12) * mm});
            skLineSegment(sketch, "E294", {"start": v(-2.38, 128.12) * mm, "end": v(-2.38, 128.27) * mm});
            skLineSegment(sketch, "E295", {"start": v(-2.38, 128.27) * mm, "end": v(-2.1, 128.73) * mm});
            skLineSegment(sketch, "E296", {"start": v(-2.1, 128.73) * mm, "end": v(-1.48, 128.97) * mm});
            skLineSegment(sketch, "E297", {"start": v(-1.48, 128.97) * mm, "end": v(-0.85, 128.78) * mm});
            skLineSegment(sketch, "E298", {"start": v(-0.85, 128.78) * mm, "end": v(-0.57, 128.28) * mm});
            skLineSegment(sketch, "E299", {"start": v(-0.57, 128.28) * mm, "end": v(-0.57, 128.12) * mm});
            skSolve(sketch);
        }
        {
            var Q0;
            {var subQ0=sQuery(id+"F22.wireOp",EDGE,"E257");Q0=makeQuery(id+"F22.imprint","IMPRINT",FACE,{"disambiguationData":[TD([[makeQuery(id+"F22.imprint","IMPRINT",EDGE,{"derivedFrom":subQ0}),1.0]])]});}
            var Q1;
            {var subQ20=sQuery(id+"F22.wireOp",EDGE,"E229");Q1=makeQuery(id+"F22.imprint","IMPRINT",FACE,{"disambiguationData":[TD([[makeQuery(id+"F22.imprint","IMPRINT",EDGE,{"derivedFrom":subQ20}),1.0]])]});}
            var Q2;
            {var subQ0=sQuery(id+"F22.wireOp",EDGE,"E215");Q2=makeQuery(id+"F22.imprint","IMPRINT",FACE,{"disambiguationData":[TD([[makeQuery(id+"F22.imprint","IMPRINT",EDGE,{"derivedFrom":subQ0}),1.0]])]});}
            var Q3;
            {var subQ0=sQuery(id+"F22.wireOp",EDGE,"E253");Q3=makeQuery(id+"F22.imprint","IMPRINT",FACE,{"disambiguationData":[TD([[makeQuery(id+"F22.imprint","IMPRINT",EDGE,{"derivedFrom":subQ0}),1.0]])]});}
            var Q4;
            {var subQ0=sQuery(id+"F22.wireOp",EDGE,"E205");Q4=makeQuery(id+"F22.imprint","IMPRINT",FACE,{"disambiguationData":[TD([[makeQuery(id+"F22.imprint","IMPRINT",EDGE,{"derivedFrom":subQ0}),1.0]])]});}
            var Q5;
            Q5=makeQuery(id+"F22.imprint","IMPRINT",FACE,{"disambiguationData":[TD([[makeQuery(id+"F22.imprint","IMPRINT",EDGE,{"derivedFrom":sQuery(id+"F22.wireOp",EDGE,"E211")}),1.0]])]});
            var Q6;
            {var subQ0=sQuery(id+"F22.wireOp",EDGE,"E203");Q6=makeQuery(id+"F22.imprint","IMPRINT",FACE,{"disambiguationData":[TD([[makeQuery(id+"F22.imprint","IMPRINT",EDGE,{"derivedFrom":subQ0}),1.0]])]});}
            var Q7;
            {var subQ0=sQuery(id+"F22.wireOp",EDGE,"E162");Q7=makeQuery(id+"F22.imprint","IMPRINT",FACE,{"disambiguationData":[TD([[makeQuery(id+"F22.imprint","IMPRINT",EDGE,{"derivedFrom":subQ0}),1.0]])]});}
            var Q8;
            Q8=makeQuery(id+"F22.imprint","IMPRINT",FACE,{"disambiguationData":[TD([[makeQuery(id+"F22.imprint","IMPRINT",EDGE,{"derivedFrom":sQuery(id+"F22.wireOp",EDGE,"E139")}),1.0]])]});
            var Q9;
            {var subQ1=sQuery(id+"F22.wireOp",EDGE,"E152");Q9=makeQuery(id+"F22.imprint","IMPRINT",FACE,{"disambiguationData":[TD([[makeQuery(id+"F22.imprint","IMPRINT",EDGE,{"derivedFrom":subQ1}),1.0]])]});}
            var Q10;
            {var subQ5=sQuery(id+"F22.wireOp",EDGE,"E166");Q10=makeQuery(id+"F22.imprint","IMPRINT",FACE,{"disambiguationData":[TD([[makeQuery(id+"F22.imprint","IMPRINT",EDGE,{"derivedFrom":subQ5}),1.0]])]});}
            var Q11;
            {var subQ15=sQuery(id+"F22.wireOp",EDGE,"E128");var subQ16=sQuery(id+"F22.wireOp",EDGE,"E127");var subQ17=makeQuery(id+"F22.imprint","INTERSECT",VERTEX,{"derivedFrom":[subQ16,subQ15]});Q11=makeQuery(id+"F22.imprint","IMPRINT",FACE,{"disambiguationData":[TD([[makeQuery(id+"F22.imprint","IMPRINT",EDGE,{"disambiguationData":[TD([[subQ17,1.0]])],"derivedFrom":subQ16}),-1.0]])]});}
            var Q12;
            {var subQ0=sQuery(id+"F22.wireOp",EDGE,"E126");Q12=makeQuery(id+"F22.imprint","IMPRINT",FACE,{"disambiguationData":[TD([[makeQuery(id+"F22.imprint","IMPRINT",EDGE,{"derivedFrom":subQ0}),-1.0]])]});}
            var Q13;
            {var subQ0=sQuery(id+"F22.wireOp",EDGE,"E129");Q13=makeQuery(id+"F22.imprint","IMPRINT",FACE,{"disambiguationData":[TD([[makeQuery(id+"F22.imprint","IMPRINT",EDGE,{"derivedFrom":subQ0}),-1.0]])]});}
            var Q14;
            {var subQ0=sQuery(id+"F22.wireOp",EDGE,"E137");Q14=makeQuery(id+"F22.imprint","IMPRINT",FACE,{"disambiguationData":[TD([[makeQuery(id+"F22.imprint","IMPRINT",EDGE,{"derivedFrom":subQ0}),-1.0]])]});}
            var Q15;
            {var subQ0=sQuery(id+"F22.wireOp",EDGE,"E134");Q15=makeQuery(id+"F22.imprint","IMPRINT",FACE,{"disambiguationData":[TD([[makeQuery(id+"F22.imprint","IMPRINT",EDGE,{"derivedFrom":subQ0}),-1.0]])]});}
            var Q16;
            {var subQ0=sQuery(id+"F22.wireOp",EDGE,"E132");Q16=makeQuery(id+"F22.imprint","IMPRINT",FACE,{"disambiguationData":[TD([[makeQuery(id+"F22.imprint","IMPRINT",EDGE,{"derivedFrom":subQ0}),-1.0]])]});}
            var Q17;
            {var subQ0=sQuery(id+"F22.wireOp",EDGE,"E115");Q17=makeQuery(id+"F22.imprint","IMPRINT",FACE,{"disambiguationData":[TD([[makeQuery(id+"F22.imprint","IMPRINT",EDGE,{"derivedFrom":subQ0}),1.0]])]});}
            var Q18;
            Q18=makeQuery(id+"F22.imprint","IMPRINT",FACE,{"disambiguationData":[TD([[makeQuery(id+"F22.imprint","IMPRINT",EDGE,{"derivedFrom":sQuery(id+"F22.wireOp",EDGE,"E123")}),1.0]])]});
            var Q19;
            {var subQ0=sQuery(id+"F22.wireOp",EDGE,"E117");Q19=makeQuery(id+"F22.imprint","IMPRINT",FACE,{"disambiguationData":[TD([[makeQuery(id+"F22.imprint","IMPRINT",EDGE,{"derivedFrom":subQ0}),1.0]])]});}
            var Q20;
            {var subQ0=sQuery(id+"F22.wireOp",EDGE,"E63");Q20=makeQuery(id+"F22.imprint","IMPRINT",FACE,{"disambiguationData":[TD([[makeQuery(id+"F22.imprint","IMPRINT",EDGE,{"derivedFrom":subQ0}),-1.0]])]});}
            var Q21;
            Q21=makeQuery(id+"F22.imprint","IMPRINT",FACE,{"disambiguationData":[TD([[makeQuery(id+"F22.imprint","IMPRINT",EDGE,{"derivedFrom":sQuery(id+"F22.wireOp",EDGE,"E31")}),-1.0]])]});
            var Q22;
            {var subQ6=sQuery(id+"F22.wireOp",EDGE,"E65");Q22=makeQuery(id+"F22.imprint","IMPRINT",FACE,{"disambiguationData":[TD([[makeQuery(id+"F22.imprint","IMPRINT",EDGE,{"derivedFrom":subQ6}),-1.0]])]});}
            var Q23;
            {var subQ0=sQuery(id+"F22.wireOp",EDGE,"E45");Q23=makeQuery(id+"F22.imprint","IMPRINT",FACE,{"disambiguationData":[TD([[makeQuery(id+"F22.imprint","IMPRINT",EDGE,{"derivedFrom":subQ0}),-1.0]])]});}
            var Q24;
            {var subQ0=sQuery(id+"F22.wireOp",EDGE,"E107");Q24=makeQuery(id+"F22.imprint","IMPRINT",FACE,{"disambiguationData":[TD([[makeQuery(id+"F22.imprint","IMPRINT",EDGE,{"derivedFrom":subQ0}),-1.0]])]});}
            extrude(context, id + "F23", {"entities" : qUnion([Q0, Q1, Q2, Q3, Q4, Q5, Q6, Q7, Q8, Q9, Q10, Q11, Q12, Q13, Q14, Q15, Q16, Q17, Q18, Q19, Q20, Q21, Q22, Q23, Q24]), "depth" : 0.5 * mm, "hasDraft" : true, "draftAngle" : 25 * degree, "draftPullDirection" : true, "hasSecondDirection" : true, "secondDirectionOppositeDirection" : true, "secondDirectionDepth" : 3 * mm, "hasSecondDirectionDraft" : true, "secondDirectionDraftAngle" : 25 * degree});
        }
    });
